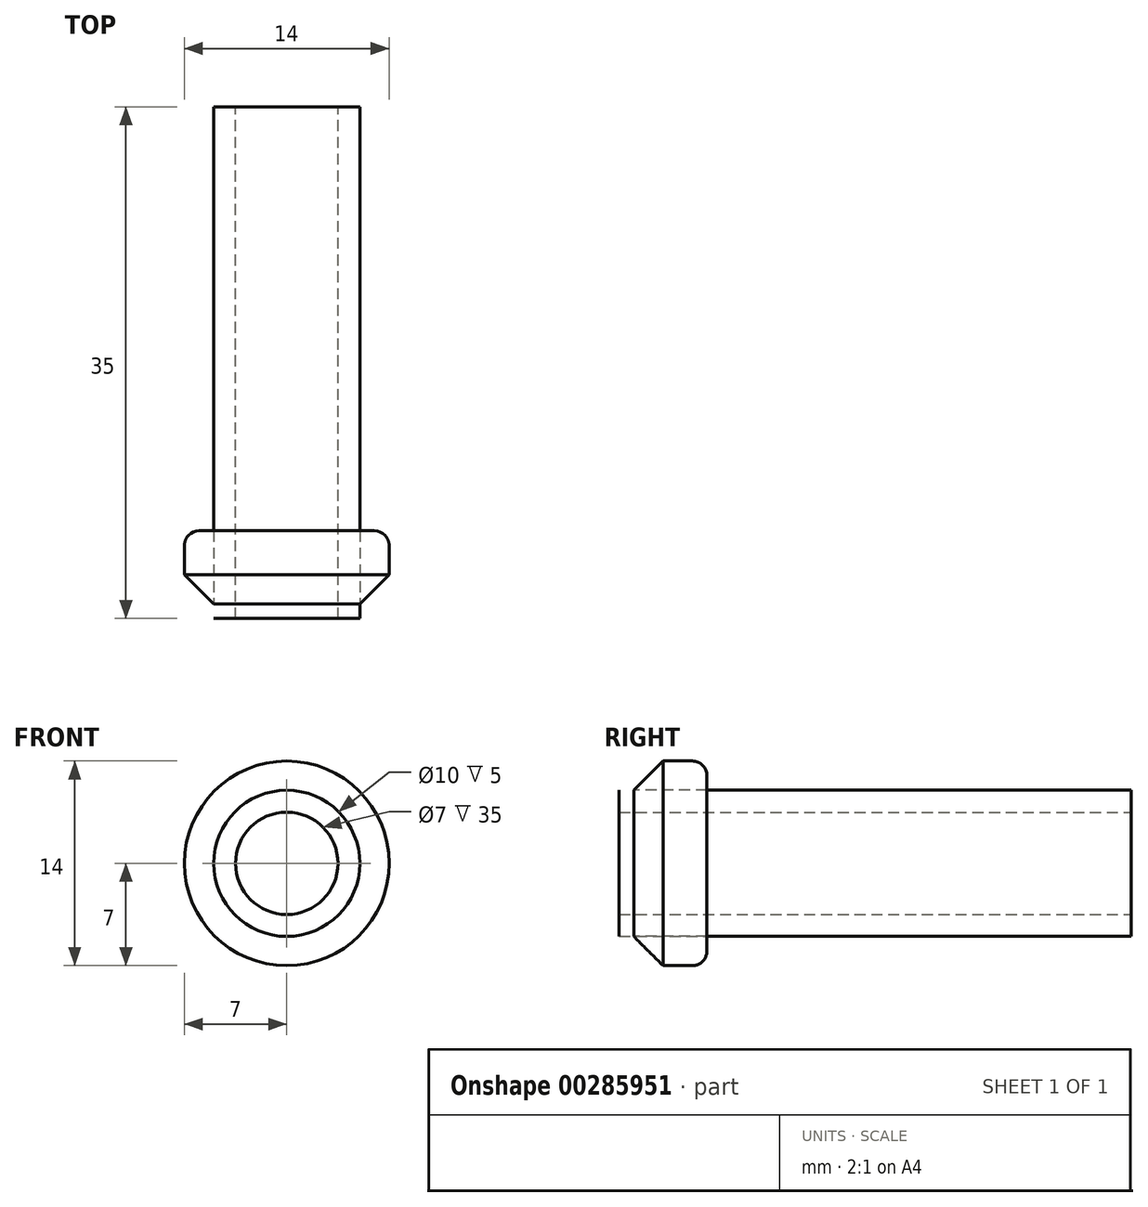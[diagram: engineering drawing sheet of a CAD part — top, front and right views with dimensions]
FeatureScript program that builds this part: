
annotation { "Feature Type Name" : "Feature", "Feature Type Description" : "" }
export const myFeature = defineFeature(function(context is Context, id is Id, definition is map)
    precondition{}
    {
        {
            var Q0;
            Q0=qCreatedBy(makeId("Front.planeOp"),FACE);
            var sketch = newSketch(context, id + "F0", { "sketchPlane" : qUnion([Q0])});
            skCircle(sketch, "E0", {"center": v(0, 0) * mm, "radius": 5 * mm});
            skCircle(sketch, "E1", {"center": v(0, 0) * mm, "radius": 3.5 * mm});
            skSolve(sketch);
        }
        {
            var Q0;
            Q0=makeQuery(id+"F0.imprint","IMPRINT",FACE,{"disambiguationData":[TD([[makeQuery(id+"F0.imprint","IMPRINT",EDGE,{"derivedFrom":sQuery(id+"F0.wireOp",EDGE,"E0")}),1.0]])]});
            extrude(context, id + "F1", {"entities" : qUnion([Q0]), "depth" : 35 * mm});
        }
        {
            var Q0;
            Q0=makeQuery(id+"F1.opExtrude","CAP_FACE",FACE,{"disambiguationData":[OSD([sQuery(id+"F0.wireOp",EDGE,"E0"),sQuery(id+"F0.wireOp",EDGE,"E1")])],"isStart":false});
            var sketch = newSketch(context, id + "F2", { "sketchPlane" : qUnion([Q0])});
            skCircle(sketch, "E2", {"center": v(0, 0) * mm, "radius": 7 * mm});
            skSolve(sketch);
        }
        {
            var Q0;
            Q0=makeQuery(id+"F2.imprint","IMPRINT",FACE,{"disambiguationData":[TD([[makeQuery(id+"F2.imprint","IMPRINT",EDGE,{"derivedFrom":sQuery(id+"F2.wireOp",EDGE,"E2")}),1.0]])]});
            extrude(context, id + "F3", {"entities" : qUnion([Q0]), "oppositeDirection" : true, "depth" : 6 * mm});
        }
        {
            var Q0;
            Q0=makeQuery(id+"F3.opExtrude","CAP_EDGE",EDGE,{"disambiguationData":[OSD([sQuery(id+"F2.wireOp",EDGE,"E2")])],"isStart":true});
            chamfer(context, id + "F4", {"entities" : qUnion([Q0]), "width" : 3 * mm, "tangentPropagation" : true});
        }
        {
            var Q0;
            Q0=makeQuery(id+"F3.opExtrude","CAP_EDGE",EDGE,{"disambiguationData":[OSD([sQuery(id+"F2.wireOp",EDGE,"E2")])],"isStart":false});
            fillet(context, id + "F5", {"entities" : qUnion([Q0]), "radius" : 1 * mm, "tangentPropagation" : true, "allowEdgeOverflow" : false});
        }
    });
